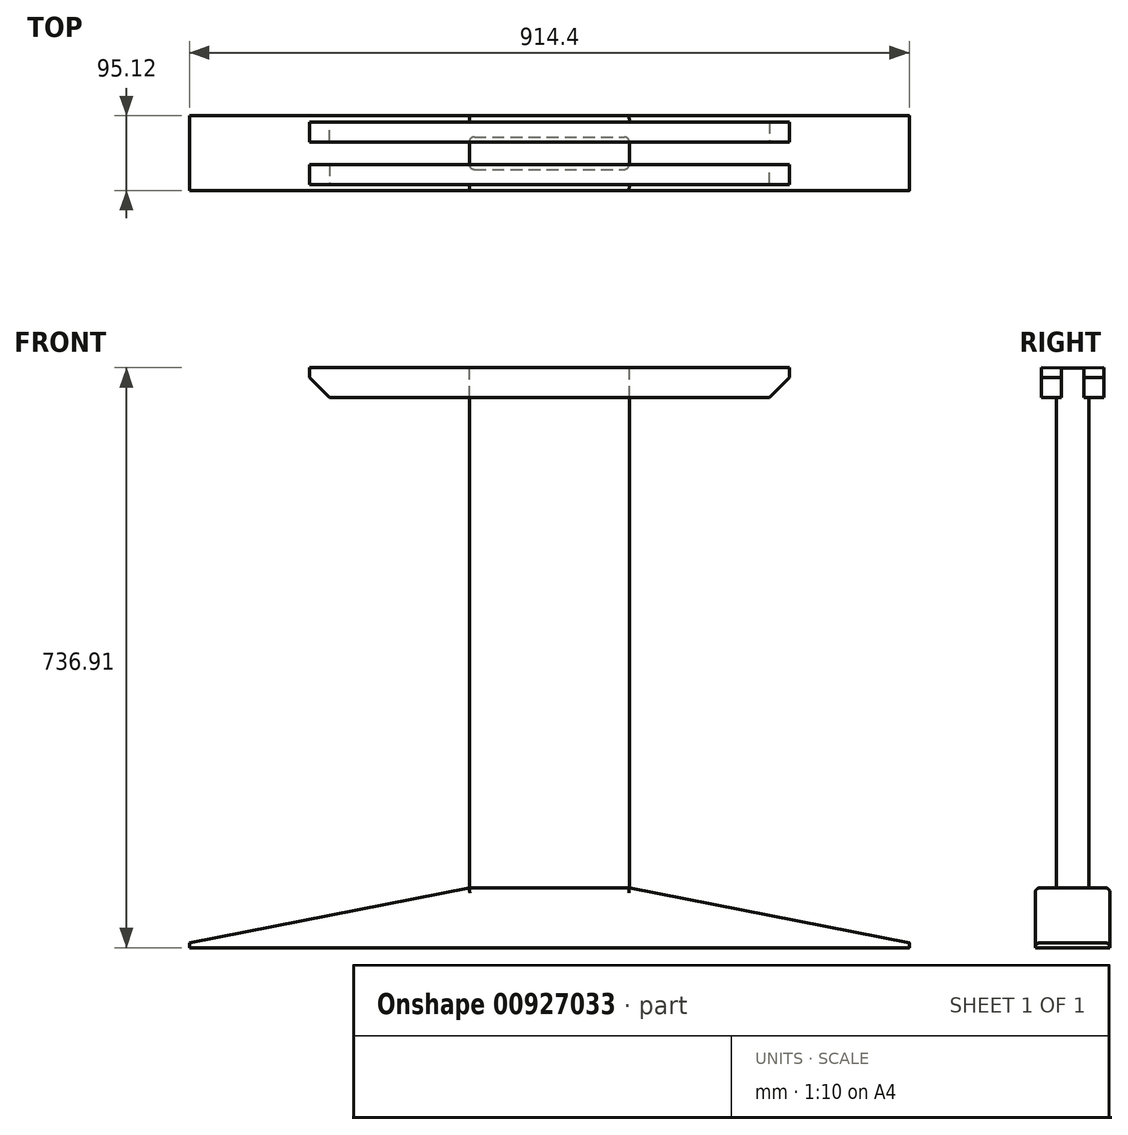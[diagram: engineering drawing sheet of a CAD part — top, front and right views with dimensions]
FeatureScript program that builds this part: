
annotation { "Feature Type Name" : "Feature", "Feature Type Description" : "" }
export const myFeature = defineFeature(function(context is Context, id is Id, definition is map)
    precondition{}
    {
        {
            var Q0;
            Q0=qCreatedBy(makeId("Front.planeOp"),FACE);
            var sketch = newSketch(context, id + "F0", { "sketchPlane" : qUnion([Q0])});
            skLineSegment(sketch, "E0", {"start": v(-457.2, -56) * mm, "end": v(0, -56) * mm});
            skLineSegment(sketch, "E1", {"start": v(-457.2, -56) * mm, "end": v(-457.2, -49.65) * mm});
            skLineSegment(sketch, "E2", {"start": v(-457.2, -49.65) * mm, "end": v(-101.6, 20.2) * mm});
            skLineSegment(sketch, "E3", {"start": v(-101.6, 20.2) * mm, "end": v(0, 20.2) * mm});
            skLineSegment(sketch, "E4", {"start": v(0, 20.2) * mm, "end": v(0, -56) * mm});
            skSolve(sketch);
        }
        {
            var Q0;
            Q0 = qSketchRegion(id + "F0", true);
            extrude(context, id + "F1", {"entities" : qUnion([Q0]), "endBound" : BoundingType.SYMMETRIC, "depth" : 1.87 * 50.8 * mm, "offsetDistance" : 25.4 * mm});
        }
        {
            var Q0;
            Q0=makeQuery(id+"F1.opExtrude","SWEPT_FACE",FACE,{"disambiguationData":[OSD([sQuery(id+"F0.wireOp",EDGE,"E3")])]});
            var sketch = newSketch(context, id + "F2", { "sketchPlane" : qUnion([Q0])});
            skLineSegment(sketch, "E5", {"start": v(-101.6, 0) * mm, "end": v(0, 0) * mm, "construction": true});
            skLineSegment(sketch, "E6.bottom", {"start": v(-101.6, 20.64) * mm, "end": v(101.6, 20.64) * mm});
            skLineSegment(sketch, "E6.top", {"start": v(-101.6, -20.64) * mm, "end": v(101.6, -20.64) * mm});
            skLineSegment(sketch, "E6.left", {"start": v(-101.6, 20.64) * mm, "end": v(-101.6, -20.64) * mm});
            skLineSegment(sketch, "E6.right", {"start": v(101.6, 20.64) * mm, "end": v(101.6, -20.64) * mm});
            skPoint(sketch, "E7", {"position": v(101.6, 0) * mm});
            skSolve(sketch);
        }
        {
            var Q0;
            Q0=makeQuery(id+"F1.opExtrude","SWEPT_BODY",BODY,{"disambiguationData":[OSD([sQuery(id+"F0.wireOp",EDGE,"E0"),sQuery(id+"F0.wireOp",EDGE,"E1"),sQuery(id+"F0.wireOp",EDGE,"E2"),sQuery(id+"F0.wireOp",EDGE,"E3"),sQuery(id+"F0.wireOp",EDGE,"E4")])]});
            var Q1;
            Q1=makeQuery(id+"F1.opExtrude","SWEPT_FACE",FACE,{"disambiguationData":[OSD([sQuery(id+"F0.wireOp",EDGE,"E4")])]});
            mirror(context, id + "F3", {"operationType" : NewBodyOperationType.ADD, "entities" : qUnion([Q0]), "mirrorPlane" : qUnion([Q1])});
        }
        {
            var Q0;
            Q0 = qSketchRegion(id + "F2", true);
            extrude(context, id + "F4", {"entities" : qUnion([Q0]), "depth" : 660.4 * mm, "offsetDistance" : 25.4 * mm});
        }
        {
            var Q0;
            Q0=qCreatedBy(makeId("Right.planeOp"),FACE);
            var sketch = newSketch(context, id + "F5", { "sketchPlane" : qUnion([Q0])});
            skLineSegment(sketch, "E8", {"start": v(14.29, 680.6) * mm, "end": v(14.29, 642.8) * mm});
            skLineSegment(sketch, "E9", {"start": v(14.29, 642.8) * mm, "end": v(39.69, 642.8) * mm});
            skLineSegment(sketch, "E10", {"start": v(39.69, 642.8) * mm, "end": v(39.69, 680.9) * mm});
            skLineSegment(sketch, "E11", {"start": v(39.69, 680.9) * mm, "end": v(14.29, 680.6) * mm});
            skSolve(sketch);
        }
        {
            var Q0;
            Q0 = qSketchRegion(id + "F5", true);
            extrude(context, id + "F6", {"entities" : qUnion([Q0]), "endBound" : BoundingType.SYMMETRIC, "depth" : 609.6 * mm, "offsetDistance" : 25.4 * mm});
        }
        {
            var Q0;
            Q0=makeQuery(id+"F6.opExtrude","SWEPT_BODY",BODY,{"disambiguationData":[OSD([sQuery(id+"F5.wireOp",EDGE,"E8"),sQuery(id+"F5.wireOp",EDGE,"E9"),sQuery(id+"F5.wireOp",EDGE,"E10"),sQuery(id+"F5.wireOp",EDGE,"E11")])]});
            var Q1;
            Q1=makeQuery(id+"F1.opExtrude","SWEPT_BODY",BODY,{"disambiguationData":[OSD([sQuery(id+"F0.wireOp",EDGE,"E0"),sQuery(id+"F0.wireOp",EDGE,"E1"),sQuery(id+"F0.wireOp",EDGE,"E2"),sQuery(id+"F0.wireOp",EDGE,"E3"),sQuery(id+"F0.wireOp",EDGE,"E4")])]});
            booleanBodies(context, id + "F7", {"operationType" : BooleanOperationType.SUBTRACTION, "tools" : qUnion([Q0]), "targets" : qUnion([Q1]), "keepTools" : true});
        }
        {
            var Q0;
            Q0=makeQuery(id+"F6.opExtrude","CAP_EDGE",EDGE,{"disambiguationData":[OSD([sQuery(id+"F5.wireOp",EDGE,"E9")])],"isStart":false});
            var Q1;
            Q1=makeQuery(id+"F6.opExtrude","CAP_EDGE",EDGE,{"disambiguationData":[OSD([sQuery(id+"F5.wireOp",EDGE,"E9")])],"isStart":true});
            chamfer(context, id + "F8", {"entities" : qUnion([Q0, Q1]), "width" : 25.4 * mm, "tangentPropagation" : true});
        }
        {
            var Q0;
            Q0=makeQuery(id+"F6.opExtrude","SWEPT_BODY",BODY,{"disambiguationData":[OSD([sQuery(id+"F5.wireOp",EDGE,"E8"),sQuery(id+"F5.wireOp",EDGE,"E9"),sQuery(id+"F5.wireOp",EDGE,"E10"),sQuery(id+"F5.wireOp",EDGE,"E11")])]});
            var Q1;
            Q1=qCreatedBy(makeId("Front.planeOp"),FACE);
            mirror(context, id + "F9", {"operationType" : NewBodyOperationType.ADD, "entities" : qUnion([Q0]), "mirrorPlane" : qUnion([Q1])});
        }
        {
            var Q0;
            {var subQ0=makeQuery(id+"F1.opExtrude","CAP_EDGE",EDGE,{"disambiguationData":[OSD([sQuery(id+"F0.wireOp",EDGE,"E3")])],"isStart":true});Q0=makeQuery(id+"F3.boolean.opBoolean","MERGE",EDGE,{"derivedFrom":[subQ0,makeQuery(id+"F3.opPattern","COPY",EDGE,{"derivedFrom":subQ0,"instanceName":"1"})]});}
            var Q1;
            Q1=makeQuery(id+"F1.opExtrude","CAP_EDGE",EDGE,{"disambiguationData":[OSD([sQuery(id+"F0.wireOp",EDGE,"E2")])],"isStart":true});
            var Q2;
            Q2=makeQuery(id+"F1.opExtrude","CAP_EDGE",EDGE,{"disambiguationData":[OSD([sQuery(id+"F0.wireOp",EDGE,"E2")])],"isStart":false});
            var Q3;
            {var subQ0=makeQuery(id+"F1.opExtrude","CAP_EDGE",EDGE,{"disambiguationData":[OSD([sQuery(id+"F0.wireOp",EDGE,"E3")])],"isStart":false});Q3=makeQuery(id+"F3.boolean.opBoolean","MERGE",EDGE,{"derivedFrom":[subQ0,makeQuery(id+"F3.opPattern","COPY",EDGE,{"derivedFrom":subQ0,"instanceName":"1"})]});}
            var Q4;
            Q4=makeQuery(id+"F3.opPattern","COPY",EDGE,{"derivedFrom":makeQuery(id+"F1.opExtrude","CAP_EDGE",EDGE,{"disambiguationData":[OSD([sQuery(id+"F0.wireOp",EDGE,"E2")])],"isStart":false}),"instanceName":"1"});
            var Q5;
            Q5=makeQuery(id+"F3.opPattern","COPY",EDGE,{"derivedFrom":makeQuery(id+"F1.opExtrude","CAP_EDGE",EDGE,{"disambiguationData":[OSD([sQuery(id+"F0.wireOp",EDGE,"E2")])],"isStart":true}),"instanceName":"1"});
            var Q6;
            Q6=makeQuery(id+"F4.opExtrude","SWEPT_EDGE",EDGE,{"disambiguationData":[OSD([sQuery(id+"F2.wireOp",EDGE,"E6.top"),sQuery(id+"F2.wireOp",EDGE,"E6.right")])]});
            var Q7;
            Q7=makeQuery(id+"F4.opExtrude","SWEPT_EDGE",EDGE,{"disambiguationData":[OSD([sQuery(id+"F2.wireOp",EDGE,"E6.bottom"),sQuery(id+"F2.wireOp",EDGE,"E6.right")])]});
            var Q8;
            Q8=makeQuery(id+"F4.opExtrude","SWEPT_EDGE",EDGE,{"disambiguationData":[OSD([sQuery(id+"F0.wireOp",EDGE,"E2"),sQuery(id+"F0.wireOp",EDGE,"E3"),sQuery(id+"F2.wireOp",EDGE,"E6.bottom"),sQuery(id+"F2.wireOp",EDGE,"E6.left")])]});
            var Q9;
            Q9=makeQuery(id+"F4.opExtrude","SWEPT_EDGE",EDGE,{"disambiguationData":[OSD([sQuery(id+"F0.wireOp",EDGE,"E2"),sQuery(id+"F0.wireOp",EDGE,"E3"),sQuery(id+"F2.wireOp",EDGE,"E6.top"),sQuery(id+"F2.wireOp",EDGE,"E6.left")])]});
            fillet(context, id + "F10", {"entities" : qUnion([Q0, Q1, Q2, Q3, Q4, Q5, Q6, Q7, Q8, Q9]), "radius" : 6.35 * mm, "tangentPropagation" : true, "allowEdgeOverflow" : false});
        }
    });
